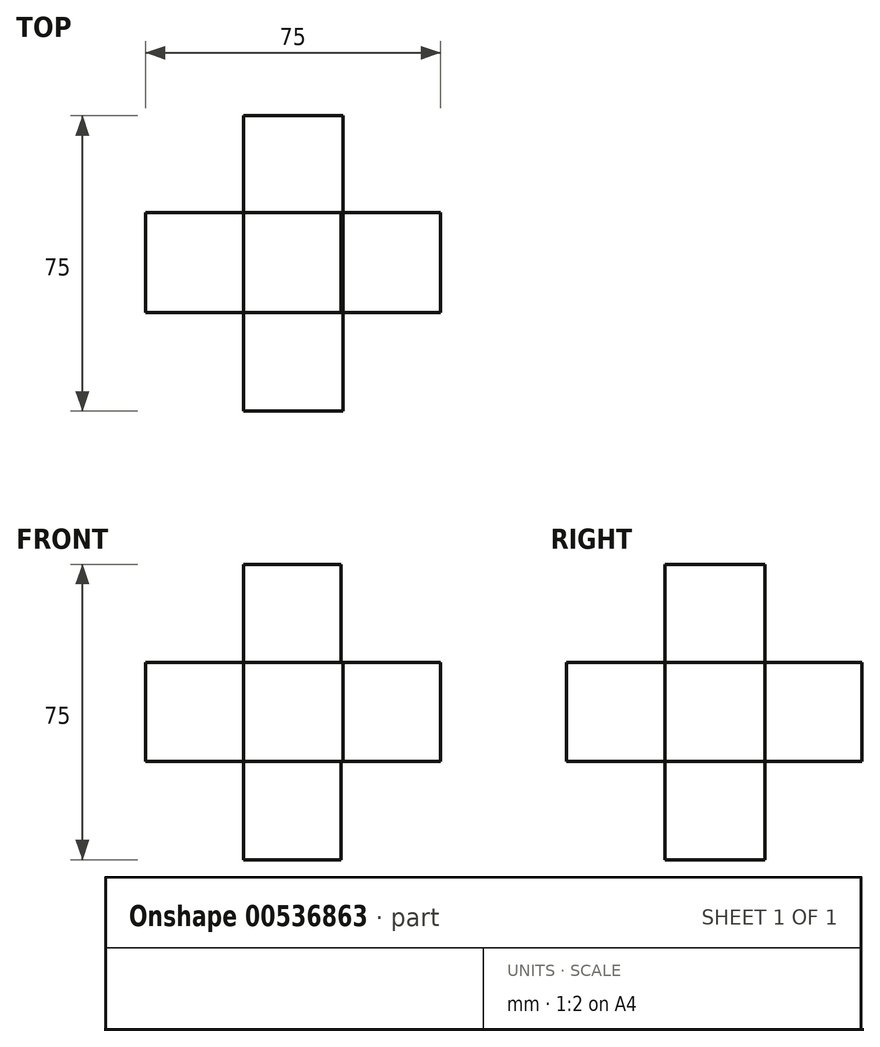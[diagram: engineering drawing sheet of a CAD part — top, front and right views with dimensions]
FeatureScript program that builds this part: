
annotation { "Feature Type Name" : "Feature", "Feature Type Description" : "" }
export const myFeature = defineFeature(function(context is Context, id is Id, definition is map)
    precondition{}
    {
        {
            var Q0;
            Q0=qCreatedBy(makeId("Front.planeOp"),FACE);
            var sketch = newSketch(context, id + "F0", { "sketchPlane" : qUnion([Q0])});
            skLineSegment(sketch, "E0.bottom", {"start": v(0, 0) * mm, "end": v(25.2, 0) * mm});
            skLineSegment(sketch, "E0.top", {"start": v(0, 25.15) * mm, "end": v(25.2, 25.15) * mm});
            skLineSegment(sketch, "E0.left", {"start": v(0, 0) * mm, "end": v(0, 25.15) * mm});
            skLineSegment(sketch, "E0.right", {"start": v(25.2, 0) * mm, "end": v(25.2, 25.15) * mm});
            skSolve(sketch);
        }
        {
            var Q0;
            Q0=makeQuery(id+"F0.imprint","IMPRINT",FACE,{"disambiguationData":[TD([[makeQuery(id+"F0.imprint","IMPRINT",EDGE,{"derivedFrom":sQuery(id+"F0.wireOp",EDGE,"E0.bottom")}),1.0]])]});
            extrude(context, id + "F1", {"entities" : qUnion([Q0]), "oppositeDirection" : true, "depth" : 50 * mm, "offsetDistance" : 25 * mm, "hasSecondDirection" : true, "secondDirectionOppositeDirection" : false, "secondDirectionDepth" : 25 * mm});
        }
        {
            var Q0;
            Q0=qCreatedBy(makeId("Top.planeOp"),FACE);
            var sketch = newSketch(context, id + "F2", { "sketchPlane" : qUnion([Q0])});
            skLineSegment(sketch, "E1.bottom", {"start": v(0, 0) * mm, "end": v(24.74, 0) * mm});
            skLineSegment(sketch, "E1.top", {"start": v(0, 25.46) * mm, "end": v(24.74, 25.46) * mm});
            skLineSegment(sketch, "E1.left", {"start": v(0, 0) * mm, "end": v(0, 25.46) * mm});
            skLineSegment(sketch, "E1.right", {"start": v(24.74, 0) * mm, "end": v(24.74, 25.46) * mm});
            skSolve(sketch);
        }
        {
            var Q0;
            Q0=makeQuery(id+"F2.imprint","IMPRINT",FACE,{"disambiguationData":[TD([[makeQuery(id+"F2.imprint","IMPRINT",EDGE,{"derivedFrom":sQuery(id+"F2.wireOp",EDGE,"E1.bottom")}),1.0]])]});
            extrude(context, id + "F3", {"entities" : qUnion([Q0]), "operationType" : NewBodyOperationType.ADD, "oppositeDirection" : true, "depth" : 25 * mm, "offsetDistance" : 25 * mm, "hasSecondDirection" : true, "secondDirectionOppositeDirection" : false, "secondDirectionDepth" : 50 * mm});
        }
        {
            var Q0;
            Q0=qCreatedBy(makeId("Right.planeOp"),FACE);
            var sketch = newSketch(context, id + "F4", { "sketchPlane" : qUnion([Q0])});
            skLineSegment(sketch, "E2.bottom", {"start": v(0, 0) * mm, "end": v(25.4, 0) * mm});
            skLineSegment(sketch, "E2.top", {"start": v(0, 25.08) * mm, "end": v(25.4, 25.08) * mm});
            skLineSegment(sketch, "E2.left", {"start": v(0, 0) * mm, "end": v(0, 25.08) * mm});
            skLineSegment(sketch, "E2.right", {"start": v(25.4, 0) * mm, "end": v(25.4, 25.08) * mm});
            skSolve(sketch);
        }
        {
            var Q0;
            Q0=makeQuery(id+"F4.imprint","IMPRINT",FACE,{"disambiguationData":[TD([[makeQuery(id+"F4.imprint","IMPRINT",EDGE,{"derivedFrom":sQuery(id+"F4.wireOp",EDGE,"E2.bottom")}),1.0]])]});
            extrude(context, id + "F5", {"entities" : qUnion([Q0]), "operationType" : NewBodyOperationType.ADD, "oppositeDirection" : true, "depth" : 25 * mm, "offsetDistance" : 25 * mm, "hasSecondDirection" : true, "secondDirectionOppositeDirection" : false, "secondDirectionDepth" : 50 * mm});
        }
    });
